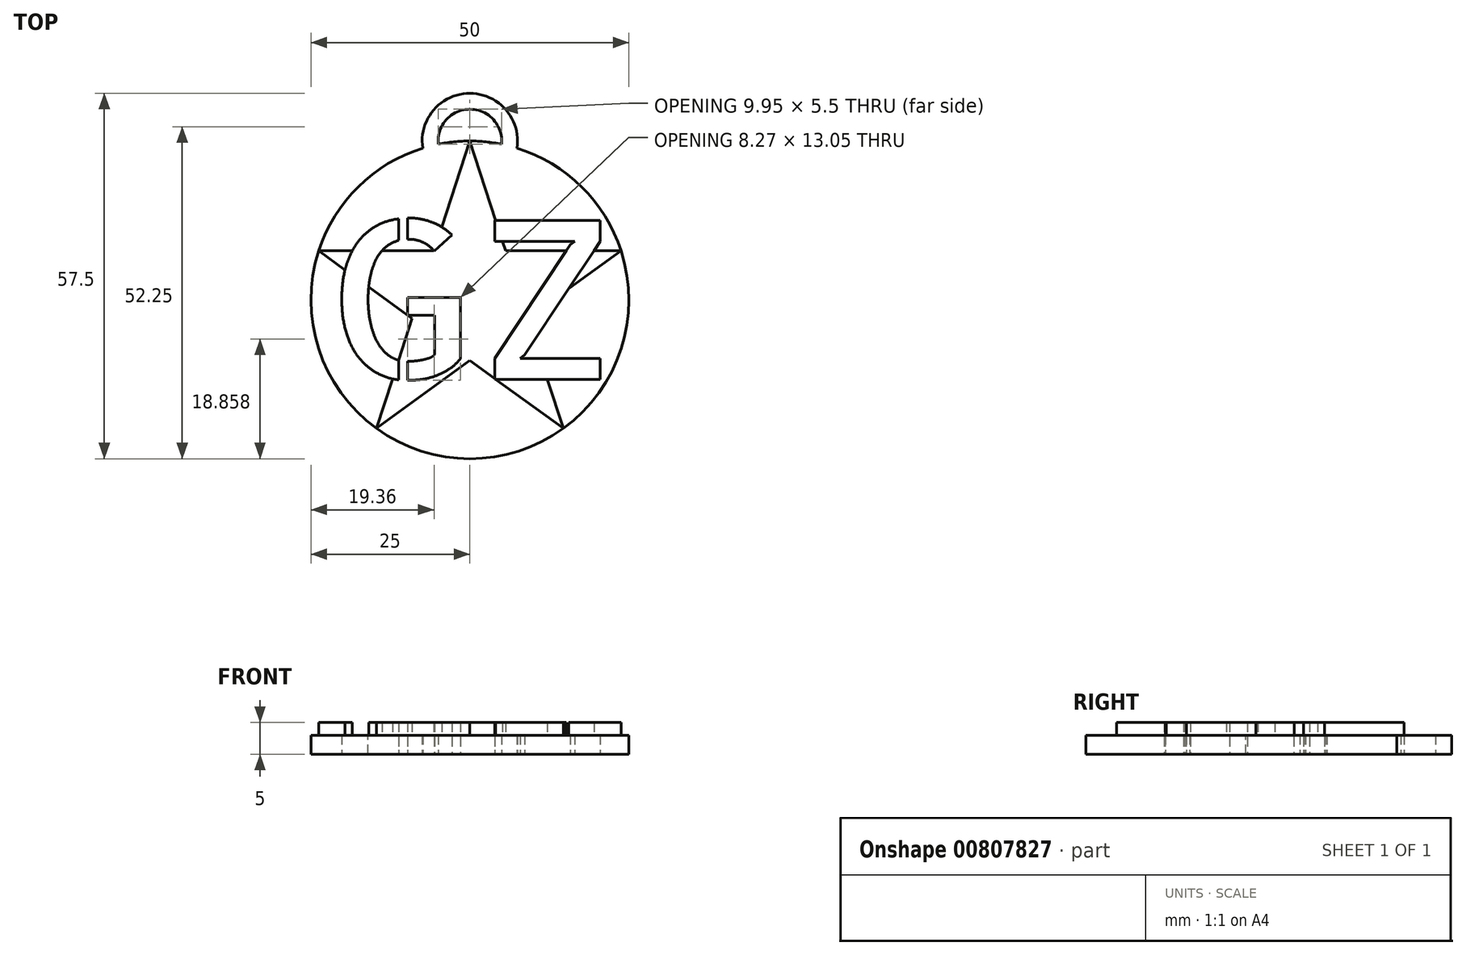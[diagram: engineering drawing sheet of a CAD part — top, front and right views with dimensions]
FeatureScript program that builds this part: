
annotation { "Feature Type Name" : "Feature", "Feature Type Description" : "" }
export const myFeature = defineFeature(function(context is Context, id is Id, definition is map)
    precondition{}
    {
        {
            var Q0;
            Q0=qCreatedBy(makeId("Top.planeOp"),FACE);
            var sketch = newSketch(context, id + "F0", { "sketchPlane" : qUnion([Q0])});
            skArc(sketch, "E0.cCircle", {"start": v(-7.42, 23.88) * mm, "mid": v(0, -25) * mm, "end": v(7.42, 23.87) * mm});
            skText(sketch, "E1", { "text": "GZ", "fontName": "AllertaStencil-Regular.ttf"});
            skLineSegment(sketch, "E2", {"start": v(-22.83, 0) * mm, "end": v(22.83, 0) * mm, "construction": true});
            skLineSegment(sketch, "E3", {"start": v(0, 25) * mm, "end": v(-5.61, 7.73) * mm});
            skLineSegment(sketch, "E4", {"start": v(-14.7, -20.23) * mm, "end": v(0, -9.55) * mm});
            skLineSegment(sketch, "E5", {"start": v(23.78, 7.73) * mm, "end": v(5.61, 7.73) * mm});
            skLineSegment(sketch, "E6", {"start": v(-23.78, 7.73) * mm, "end": v(-9.08, -2.95) * mm});
            skLineSegment(sketch, "E7", {"start": v(14.7, -20.23) * mm, "end": v(9.08, -2.95) * mm});
            skLineSegment(sketch, "E8.trimOffspring", {"start": v(-9.08, -2.95) * mm, "end": v(-14.7, -20.23) * mm});
            skLineSegment(sketch, "E9.trimOffspring", {"start": v(-5.61, 7.73) * mm, "end": v(-23.78, 7.73) * mm});
            skLineSegment(sketch, "E10.trimOffspring", {"start": v(5.61, 7.73) * mm, "end": v(0, 25) * mm});
            skLineSegment(sketch, "E11.trimOffspring", {"start": v(9.08, -2.95) * mm, "end": v(23.78, 7.73) * mm});
            skLineSegment(sketch, "E12.trimOffspring", {"start": v(0, -9.55) * mm, "end": v(14.7, -20.23) * mm});
            skArc(sketch, "E13", {"start": v(7.42, 23.87) * mm, "mid": v(0, 32.5) * mm, "end": v(-7.42, 23.88) * mm});
            skArc(sketch, "E14", {"start": v(4.97, 24.5) * mm, "mid": v(0, 30) * mm, "end": v(-4.97, 24.5) * mm});
            skArc(sketch, "E15.trimOffspring", {"start": v(4.97, 24.5) * mm, "mid": v(0, 25) * mm, "end": v(-4.97, 24.5) * mm});
            const initialGuessF0  = {"E1": [-0.02283, -0.0125, 1, 0, 0.025]};
            skSetInitialGuess(sketch, initialGuessF0);
            skSolve(sketch);
        }
        {
            var Q0;
            {var subQ12=sQuery(id+"F0.wireOp",EDGE,"E1.sketch_text.stroke-1");Q0=makeQuery(id+"F0.imprint","IMPRINT",FACE,{"disambiguationData":[TD([[makeQuery(id+"F0.imprint","IMPRINT",EDGE,{"derivedFrom":subQ12}),1.0]])]});}
            var Q1;
            {var subQ15=sQuery(id+"F0.wireOp",EDGE,"E1.sketch_text.stroke-7");Q1=makeQuery(id+"F0.imprint","IMPRINT",FACE,{"disambiguationData":[TD([[makeQuery(id+"F0.imprint","IMPRINT",EDGE,{"derivedFrom":subQ15}),1.0]])]});}
            var Q2;
            {var subQ0=sQuery(id+"F0.wireOp",EDGE,"E1.sketch_text.stroke-9");var subQ1=sQuery(id+"F0.wireOp",EDGE,"E1.sketch_text.stroke-8");var subQ2=makeQuery(id+"F0.imprint","INTERSECT",VERTEX,{"derivedFrom":[subQ1,subQ0]});Q2=makeQuery(id+"F0.imprint","IMPRINT",FACE,{"disambiguationData":[TD([[makeQuery(id+"F0.imprint","IMPRINT",EDGE,{"disambiguationData":[TD([[subQ2,1.0]])],"derivedFrom":subQ1}),1.0]])]});}
            var Q3;
            {var subQ0=sQuery(id+"F0.wireOp",EDGE,"E1.sketch_text.stroke-23");Q3=makeQuery(id+"F0.imprint","IMPRINT",FACE,{"disambiguationData":[TD([[makeQuery(id+"F0.imprint","IMPRINT",EDGE,{"derivedFrom":subQ0}),1.0]])]});}
            var Q4;
            {var subQ6=sQuery(id+"F0.wireOp",EDGE,"E1.sketch_text.stroke-17");Q4=makeQuery(id+"F0.imprint","IMPRINT",FACE,{"disambiguationData":[TD([[makeQuery(id+"F0.imprint","IMPRINT",EDGE,{"derivedFrom":subQ6}),1.0]])]});}
            var Q5;
            {var subQ6=sQuery(id+"F0.wireOp",EDGE,"E4");Q5=makeQuery(id+"F0.imprint","IMPRINT",FACE,{"disambiguationData":[TD([[makeQuery(id+"F0.imprint","IMPRINT",EDGE,{"derivedFrom":subQ6}),-1.0]])]});}
            var Q6;
            {var subQ0=sQuery(id+"F0.wireOp",EDGE,"E7");var subQ1=sQuery(id+"F0.wireOp",EDGE,"E1.sketch_text.stroke-46");var subQ2=makeQuery(id+"F0.imprint","INTERSECT",VERTEX,{"derivedFrom":[subQ1,subQ0]});Q6=makeQuery(id+"F0.imprint","IMPRINT",FACE,{"disambiguationData":[TD([[makeQuery(id+"F0.imprint","IMPRINT",EDGE,{"disambiguationData":[TD([[subQ2,-1.0]])],"derivedFrom":subQ1}),1.0]])]});}
            var Q7;
            {var subQ0=sQuery(id+"F0.wireOp",EDGE,"E1.sketch_text.stroke-45");Q7=makeQuery(id+"F0.imprint","IMPRINT",FACE,{"disambiguationData":[TD([[makeQuery(id+"F0.imprint","IMPRINT",EDGE,{"derivedFrom":subQ0}),1.0]])]});}
            var Q8;
            {var subQ0=sQuery(id+"F0.wireOp",EDGE,"E1.sketch_text.stroke-43");Q8=makeQuery(id+"F0.imprint","IMPRINT",FACE,{"disambiguationData":[TD([[makeQuery(id+"F0.imprint","IMPRINT",EDGE,{"derivedFrom":subQ0}),1.0]])]});}
            var Q9;
            {var subQ0=sQuery(id+"F0.wireOp",EDGE,"E5");var subQ1=sQuery(id+"F0.wireOp",EDGE,"E1.sketch_text.stroke-42");var subQ2=makeQuery(id+"F0.imprint","INTERSECT",VERTEX,{"derivedFrom":[subQ1,subQ0]});Q9=makeQuery(id+"F0.imprint","IMPRINT",FACE,{"disambiguationData":[TD([[makeQuery(id+"F0.imprint","IMPRINT",EDGE,{"disambiguationData":[TD([[subQ2,-1.0]])],"derivedFrom":subQ1}),1.0]])]});}
            var Q10;
            {var subQ0=sQuery(id+"F0.wireOp",EDGE,"E1.sketch_text.stroke-41");Q10=makeQuery(id+"F0.imprint","IMPRINT",FACE,{"disambiguationData":[TD([[makeQuery(id+"F0.imprint","IMPRINT",EDGE,{"derivedFrom":subQ0}),1.0]])]});}
            var Q11;
            {var subQ5=sQuery(id+"F0.wireOp",EDGE,"E1.sketch_text.stroke-49");Q11=makeQuery(id+"F0.imprint","IMPRINT",FACE,{"disambiguationData":[TD([[makeQuery(id+"F0.imprint","IMPRINT",EDGE,{"derivedFrom":subQ5}),1.0]])]});}
            extrude(context, id + "F1", {"entities" : qUnion([Q0, Q1, Q2, Q3, Q4, Q5, Q6, Q7, Q8, Q9, Q10, Q11]), "depth" : 3 * mm, "offsetDistance" : 25 * mm});
        }
        {
            var Q0;
            {var subQ15=sQuery(id+"F0.wireOp",EDGE,"E1.sketch_text.stroke-7");Q0=makeQuery(id+"F0.imprint","IMPRINT",FACE,{"disambiguationData":[TD([[makeQuery(id+"F0.imprint","IMPRINT",EDGE,{"derivedFrom":subQ15}),1.0]])]});}
            var Q1;
            {var subQ0=sQuery(id+"F0.wireOp",EDGE,"E1.sketch_text.stroke-9");var subQ1=sQuery(id+"F0.wireOp",EDGE,"E1.sketch_text.stroke-8");var subQ2=makeQuery(id+"F0.imprint","INTERSECT",VERTEX,{"derivedFrom":[subQ1,subQ0]});Q1=makeQuery(id+"F0.imprint","IMPRINT",FACE,{"disambiguationData":[TD([[makeQuery(id+"F0.imprint","IMPRINT",EDGE,{"disambiguationData":[TD([[subQ2,1.0]])],"derivedFrom":subQ1}),1.0]])]});}
            var Q2;
            {var subQ0=sQuery(id+"F0.wireOp",EDGE,"E7");var subQ1=sQuery(id+"F0.wireOp",EDGE,"E1.sketch_text.stroke-46");var subQ2=makeQuery(id+"F0.imprint","INTERSECT",VERTEX,{"derivedFrom":[subQ1,subQ0]});Q2=makeQuery(id+"F0.imprint","IMPRINT",FACE,{"disambiguationData":[TD([[makeQuery(id+"F0.imprint","IMPRINT",EDGE,{"disambiguationData":[TD([[subQ2,-1.0]])],"derivedFrom":subQ1}),1.0]])]});}
            var Q3;
            {var subQ0=sQuery(id+"F0.wireOp",EDGE,"E5");var subQ1=sQuery(id+"F0.wireOp",EDGE,"E1.sketch_text.stroke-42");var subQ2=makeQuery(id+"F0.imprint","INTERSECT",VERTEX,{"derivedFrom":[subQ1,subQ0]});Q3=makeQuery(id+"F0.imprint","IMPRINT",FACE,{"disambiguationData":[TD([[makeQuery(id+"F0.imprint","IMPRINT",EDGE,{"disambiguationData":[TD([[subQ2,-1.0]])],"derivedFrom":subQ1}),1.0]])]});}
            extrude(context, id + "F2", {"entities" : qUnion([Q0, Q1, Q2, Q3]), "operationType" : NewBodyOperationType.ADD, "depth" : 5 * mm, "offsetDistance" : 25 * mm});
        }
    });
